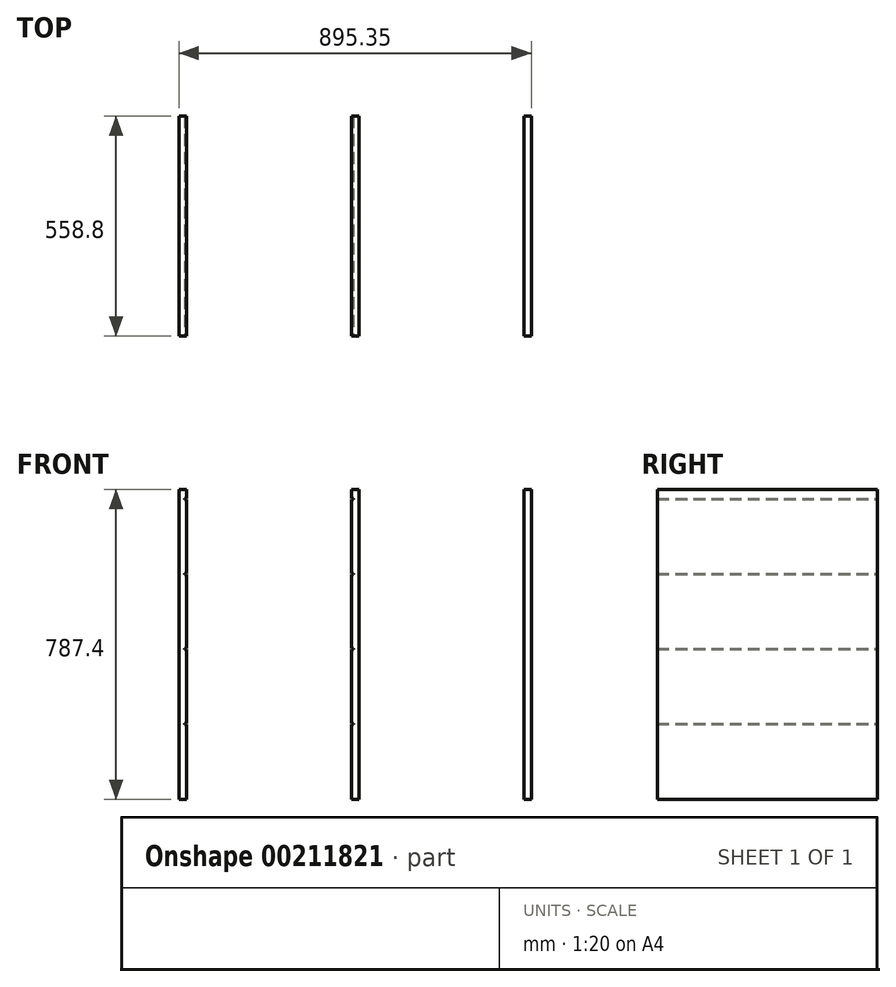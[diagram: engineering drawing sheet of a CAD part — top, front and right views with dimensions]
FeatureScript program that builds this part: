
annotation { "Feature Type Name" : "Feature", "Feature Type Description" : "" }
export const myFeature = defineFeature(function(context is Context, id is Id, definition is map)
    precondition{}
    {
        {
            var Q0;
            Q0=qCreatedBy(makeId("Front.planeOp"),FACE);
            var sketch = newSketch(context, id + "F0", { "sketchPlane" : qUnion([Q0])});
            skLineSegment(sketch, "E0.bottom", {"start": v(0, 0) * mm, "end": v(19.05, 0) * mm});
            skLineSegment(sketch, "E0.top", {"start": v(0, 787.4) * mm, "end": v(19.05, 787.4) * mm});
            skLineSegment(sketch, "E0.left", {"start": v(0, 0) * mm, "end": v(0, 787.4) * mm});
            skLineSegment(sketch, "E0.right", {"start": v(19.05, 0) * mm, "end": v(19.05, 787.4) * mm});
            skLineSegment(sketch, "E1.bottom", {"start": v(438.15, 0) * mm, "end": v(457.2, 0) * mm});
            skLineSegment(sketch, "E1.top", {"start": v(438.15, 787.4) * mm, "end": v(457.2, 787.4) * mm});
            skLineSegment(sketch, "E1.left", {"start": v(438.15, 0) * mm, "end": v(438.15, 787.4) * mm});
            skLineSegment(sketch, "E1.right", {"start": v(457.2, 0) * mm, "end": v(457.2, 787.4) * mm});
            skLineSegment(sketch, "E2.bottom", {"start": v(895.35, 0) * mm, "end": v(876.3, 0) * mm});
            skLineSegment(sketch, "E2.top", {"start": v(895.35, 787.4) * mm, "end": v(876.3, 787.4) * mm});
            skLineSegment(sketch, "E2.left", {"start": v(895.35, 0) * mm, "end": v(895.35, 787.4) * mm});
            skLineSegment(sketch, "E2.right", {"start": v(876.3, 0) * mm, "end": v(876.3, 787.4) * mm});
            skLineSegment(sketch, "E3", {"start": v(19.05, 0) * mm, "end": v(438.15, 0) * mm, "construction": true});
            skLineSegment(sketch, "E4", {"start": v(457.2, 0) * mm, "end": v(876.3, 0) * mm, "construction": true});
            skSolve(sketch);
        }
        {
            var Q0;
            Q0 = qSketchRegion(id + "F0", true);
            extrude(context, id + "F1", {"entities" : qUnion([Q0]), "oppositeDirection" : true, "depth" : 558.8 * mm});
        }
        {
            var Q0;
            Q0=qCreatedBy(makeId("Front.planeOp"),FACE);
            var sketch = newSketch(context, id + "F2", { "sketchPlane" : qUnion([Q0])});
            skLineSegment(sketch, "E5.bottom", {"start": v(14.29, 193.67) * mm, "end": v(442.91, 193.67) * mm});
            skLineSegment(sketch, "E5.top", {"start": v(14.29, 190.5) * mm, "end": v(442.91, 190.5) * mm});
            skLineSegment(sketch, "E5.left", {"start": v(14.29, 193.68) * mm, "end": v(14.29, 190.5) * mm});
            skLineSegment(sketch, "E5.right", {"start": v(442.91, 193.67) * mm, "end": v(442.91, 190.5) * mm});
            skLineSegment(sketch, "E6", {"start": v(228.6, 0) * mm, "end": v(228.6, 12.7) * mm, "construction": true});
            skLineSegment(sketch, "E7", {"start": v(228.6, 12.7) * mm, "end": v(228.6, 190.5) * mm, "construction": true});
            skLineSegment(sketch, "E8.0.1.0", {"start": v(228.6, 203.2) * mm, "end": v(228.6, 381) * mm, "construction": true});
            skLineSegment(sketch, "E8.0.1.1", {"start": v(14.29, 381) * mm, "end": v(442.91, 381) * mm});
            skLineSegment(sketch, "E8.0.1.2", {"start": v(14.29, 384.18) * mm, "end": v(442.91, 384.18) * mm});
            skLineSegment(sketch, "E8.0.1.3", {"start": v(228.6, 190.5) * mm, "end": v(228.6, 203.2) * mm, "construction": true});
            skLineSegment(sketch, "E8.0.1.4", {"start": v(442.91, 384.18) * mm, "end": v(442.91, 381) * mm});
            skLineSegment(sketch, "E8.0.1.5", {"start": v(14.29, 384.18) * mm, "end": v(14.29, 381) * mm});
            skLineSegment(sketch, "E8.0.2.0", {"start": v(228.6, 393.7) * mm, "end": v(228.6, 571.5) * mm, "construction": true});
            skLineSegment(sketch, "E8.0.2.1", {"start": v(14.29, 571.5) * mm, "end": v(442.91, 571.5) * mm});
            skLineSegment(sketch, "E8.0.2.2", {"start": v(14.29, 574.68) * mm, "end": v(442.91, 574.68) * mm});
            skLineSegment(sketch, "E8.0.2.3", {"start": v(228.6, 381) * mm, "end": v(228.6, 393.7) * mm, "construction": true});
            skLineSegment(sketch, "E8.0.2.4", {"start": v(442.91, 574.68) * mm, "end": v(442.91, 571.5) * mm});
            skLineSegment(sketch, "E8.0.2.5", {"start": v(14.29, 574.68) * mm, "end": v(14.29, 571.5) * mm});
            skLineSegment(sketch, "E8.direction1", {"start": v(-52.98, 190.5) * mm, "end": v(14.29, 190.5) * mm, "construction": true});
            skLineSegment(sketch, "E8.direction2", {"start": v(14.29, 190.5) * mm, "end": v(14.29, 381) * mm, "construction": true});
            skLineSegment(sketch, "E9.0.0.3", {"start": v(228.6, 584.2) * mm, "end": v(228.6, 762) * mm, "construction": true});
            skLineSegment(sketch, "E9.3.0.3", {"start": v(14.29, 762) * mm, "end": v(442.91, 762) * mm});
            skLineSegment(sketch, "E9.6.0.3", {"start": v(14.29, 765.18) * mm, "end": v(442.91, 765.18) * mm});
            skLineSegment(sketch, "E9.9.0.3", {"start": v(228.6, 571.5) * mm, "end": v(228.6, 584.2) * mm, "construction": true});
            skLineSegment(sketch, "E9.12.0.3", {"start": v(442.91, 765.18) * mm, "end": v(442.91, 762) * mm});
            skLineSegment(sketch, "E9.15.0.3", {"start": v(14.29, 765.18) * mm, "end": v(14.29, 762) * mm});
            skSolve(sketch);
        }
        {
            var Q0;
            Q0 = qSketchRegion(id + "F2", true);
            extrude(context, id + "F3", {"entities" : qUnion([Q0]), "operationType" : NewBodyOperationType.REMOVE, "endBound" : BoundingType.THROUGH_ALL, "oppositeDirection" : true, "depth" : 25.4 * mm});
        }
    });
